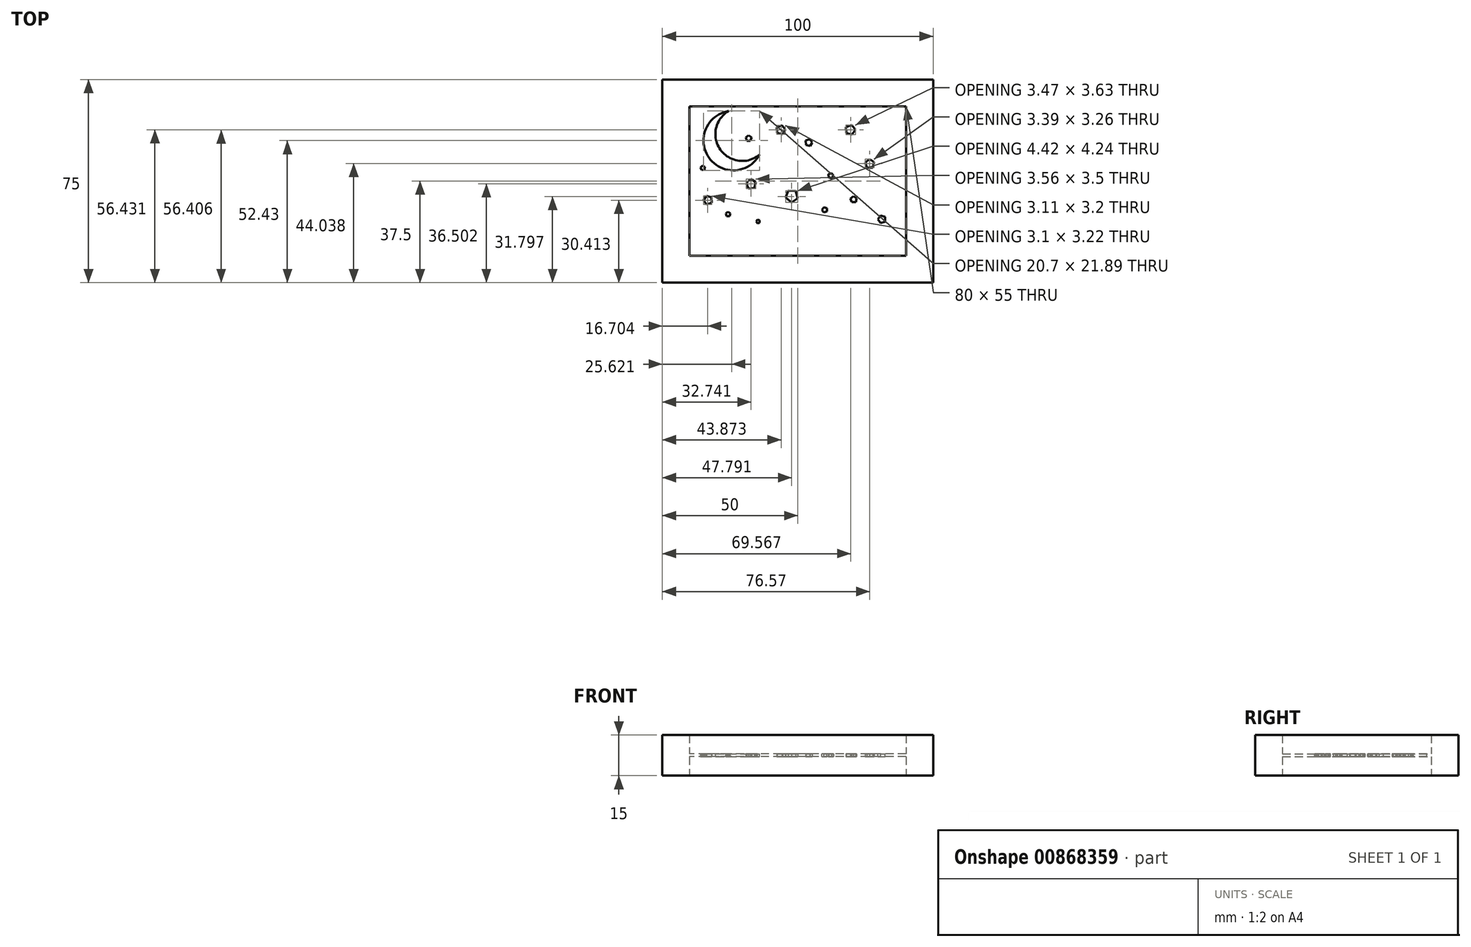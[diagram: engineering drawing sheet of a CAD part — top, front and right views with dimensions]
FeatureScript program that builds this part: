
annotation { "Feature Type Name" : "Feature", "Feature Type Description" : "" }
export const myFeature = defineFeature(function(context is Context, id is Id, definition is map)
    precondition{}
    {
        {
            var Q0;
            Q0=qCreatedBy(makeId("Top.planeOp"),FACE);
            var sketch = newSketch(context, id + "F0", { "sketchPlane" : qUnion([Q0])});
            skLineSegment(sketch, "E0.bottom", {"start": v(50, -37.5) * mm, "end": v(-50, -37.5) * mm});
            skLineSegment(sketch, "E0.top", {"start": v(50, 37.5) * mm, "end": v(-50, 37.5) * mm});
            skLineSegment(sketch, "E0.left", {"start": v(50, -37.5) * mm, "end": v(50, 37.5) * mm});
            skLineSegment(sketch, "E0.right", {"start": v(-50, -37.5) * mm, "end": v(-50, 37.5) * mm});
            skPoint(sketch, "E0.middle", {"position": v(0, 0) * mm});
            skLineSegment(sketch, "E1.bottom", {"start": v(40, -27.5) * mm, "end": v(-40, -27.5) * mm});
            skLineSegment(sketch, "E1.top", {"start": v(40, 27.5) * mm, "end": v(-40, 27.5) * mm});
            skLineSegment(sketch, "E1.left", {"start": v(40, -27.5) * mm, "end": v(40, 27.5) * mm});
            skLineSegment(sketch, "E1.right", {"start": v(-40, -27.5) * mm, "end": v(-40, 27.5) * mm});
            skSolve(sketch);
        }
        {
            var Q0;
            Q0=makeQuery(id+"F0.imprint","IMPRINT",FACE,{"disambiguationData":[TD([[makeQuery(id+"F0.imprint","IMPRINT",EDGE,{"derivedFrom":sQuery(id+"F0.wireOp",EDGE,"E0.bottom")}),-1.0]])]});
            extrude(context, id + "F1", {"entities" : qUnion([Q0]), "endBound" : BoundingType.SYMMETRIC, "depth" : 15 * mm, "offsetDistance" : 25 * mm});
        }
        {
            var Q0;
            Q0=qCreatedBy(makeId("Top.planeOp"),FACE);
            var sketch = newSketch(context, id + "F2", { "sketchPlane" : qUnion([Q0])});
            skLineSegment(sketch, "E2.bottom", {"start": v(42.5, -30) * mm, "end": v(-42.5, -30) * mm});
            skLineSegment(sketch, "E2.top", {"start": v(42.5, 30) * mm, "end": v(-42.5, 30) * mm});
            skLineSegment(sketch, "E2.left", {"start": v(42.5, -30) * mm, "end": v(42.5, 30) * mm});
            skLineSegment(sketch, "E2.right", {"start": v(-42.5, -30) * mm, "end": v(-42.5, 30) * mm});
            skPoint(sketch, "E2.middle", {"position": v(0, 0) * mm});
            skSolve(sketch);
        }
        {
            var Q0;
            Q0 = qSketchRegion(id + "F2", true);
            extrude(context, id + "F3", {"entities" : qUnion([Q0]), "operationType" : NewBodyOperationType.ADD, "endBound" : BoundingType.SYMMETRIC, "depth" : 1 * mm, "offsetDistance" : 25 * mm});
        }
        {
            var Q0;
            Q0=makeQuery(id+"F3.opExtrude","CAP_FACE",FACE,{"disambiguationData":[OSD([sQuery(id+"F2.wireOp",EDGE,"E2.bottom"),sQuery(id+"F2.wireOp",EDGE,"E2.top"),sQuery(id+"F2.wireOp",EDGE,"E2.left"),sQuery(id+"F2.wireOp",EDGE,"E2.right")])],"isStart":false});
            var sketch = newSketch(context, id + "F4", { "sketchPlane" : qUnion([Q0])});
            skCircle(sketch, "E3", {"center": v(-23.77, 14.99) * mm, "radius": 11.02 * mm});
            skCircle(sketch, "E4", {"center": v(-20.49, 17.33) * mm, "radius": 9.9 * mm});
            skSolve(sketch);
        }
        {
            var Q0;
            {var subQ0=sQuery(id+"F4.wireOp",EDGE,"E4");var subQ1=sQuery(id+"F4.wireOp",EDGE,"E3");var subQ2=makeQuery(id+"F4.imprint","INTERSECT",VERTEX,{"disambiguationData":[OD(0.0)],"derivedFrom":[subQ1,subQ0]});Q0=makeQuery(id+"F4.imprint","IMPRINT",FACE,{"disambiguationData":[TD([[makeQuery(id+"F4.imprint","IMPRINT",EDGE,{"disambiguationData":[TD([[subQ2,-1.0]])],"derivedFrom":subQ1}),1.0]])]});}
            extrude(context, id + "F5", {"entities" : qUnion([Q0]), "operationType" : NewBodyOperationType.REMOVE, "endBound" : BoundingType.SYMMETRIC, "oppositeDirection" : true, "depth" : 8 * mm, "offsetDistance" : 25 * mm});
        }
        {
            var Q0;
            Q0=makeQuery(id+"F3.opExtrude","CAP_FACE",FACE,{"disambiguationData":[OSD([sQuery(id+"F2.wireOp",EDGE,"E2.bottom"),sQuery(id+"F2.wireOp",EDGE,"E2.top"),sQuery(id+"F2.wireOp",EDGE,"E2.left"),sQuery(id+"F2.wireOp",EDGE,"E2.right")])],"isStart":false});
            var sketch = newSketch(context, id + "F6", { "sketchPlane" : qUnion([Q0])});
            skCircle(sketch, "E5.cCircle", {"center": v(-6.25, 18.9) * mm, "radius": 1.68 * mm, "construction": true});
            skLineSegment(sketch, "E5.0", {"start": v(-5.63, 17.33) * mm, "end": v(-7.55, 17.82) * mm});
            skLineSegment(sketch, "E5.1", {"start": v(-7.55, 17.82) * mm, "end": v(-7.68, 19.8) * mm});
            skLineSegment(sketch, "E5.2", {"start": v(-7.68, 19.8) * mm, "end": v(-5.84, 20.53) * mm});
            skLineSegment(sketch, "E5.3", {"start": v(-5.84, 20.53) * mm, "end": v(-4.57, 19) * mm});
            skLineSegment(sketch, "E5.4", {"start": v(-4.57, 19) * mm, "end": v(-5.63, 17.33) * mm});
            skCircle(sketch, "E6.cCircle", {"center": v(4.07, 14.2) * mm, "radius": 1.34 * mm, "construction": true});
            skLineSegment(sketch, "E6.0", {"start": v(4.54, 12.95) * mm, "end": v(3.02, 13.37) * mm});
            skLineSegment(sketch, "E6.1", {"start": v(3.02, 13.37) * mm, "end": v(2.95, 14.94) * mm});
            skLineSegment(sketch, "E6.2", {"start": v(2.95, 14.94) * mm, "end": v(4.42, 15.5) * mm});
            skLineSegment(sketch, "E6.3", {"start": v(4.42, 15.5) * mm, "end": v(5.4, 14.26) * mm});
            skLineSegment(sketch, "E6.4", {"start": v(5.4, 14.26) * mm, "end": v(4.54, 12.95) * mm});
            skCircle(sketch, "E7.cCircle", {"center": v(19.4, 18.9) * mm, "radius": 1.9 * mm, "construction": true});
            skLineSegment(sketch, "E7.0", {"start": v(17.83, 20) * mm, "end": v(19.95, 20.72) * mm});
            skLineSegment(sketch, "E7.1", {"start": v(19.95, 20.72) * mm, "end": v(21.3, 18.93) * mm});
            skLineSegment(sketch, "E7.2", {"start": v(21.3, 18.93) * mm, "end": v(20.02, 17.1) * mm});
            skLineSegment(sketch, "E7.3", {"start": v(20.02, 17.1) * mm, "end": v(17.87, 17.75) * mm});
            skLineSegment(sketch, "E7.4", {"start": v(17.87, 17.75) * mm, "end": v(17.83, 20) * mm});
            skCircle(sketch, "E8.cCircle", {"center": v(26.59, 6.38) * mm, "radius": 1.78 * mm, "construction": true});
            skLineSegment(sketch, "E8.0", {"start": v(27.68, 4.98) * mm, "end": v(25.59, 4.9) * mm});
            skLineSegment(sketch, "E8.1", {"start": v(25.59, 4.9) * mm, "end": v(24.88, 6.88) * mm});
            skLineSegment(sketch, "E8.2", {"start": v(24.88, 6.88) * mm, "end": v(26.53, 8.17) * mm});
            skLineSegment(sketch, "E8.3", {"start": v(26.53, 8.17) * mm, "end": v(28.27, 7) * mm});
            skLineSegment(sketch, "E8.4", {"start": v(28.27, 7) * mm, "end": v(27.68, 4.98) * mm});
            skCircle(sketch, "E9.cCircle", {"center": v(12.2, 2) * mm, "radius": 1 * mm, "construction": true});
            skLineSegment(sketch, "E9.0", {"start": v(11.42, 1.38) * mm, "end": v(11.36, 2.56) * mm});
            skLineSegment(sketch, "E9.1", {"start": v(11.36, 2.56) * mm, "end": v(12.47, 2.97) * mm});
            skLineSegment(sketch, "E9.2", {"start": v(12.47, 2.97) * mm, "end": v(13.2, 2.05) * mm});
            skLineSegment(sketch, "E9.3", {"start": v(13.2, 2.05) * mm, "end": v(12.55, 1.07) * mm});
            skLineSegment(sketch, "E9.4", {"start": v(12.55, 1.07) * mm, "end": v(11.42, 1.38) * mm});
            skCircle(sketch, "E10.cCircle", {"center": v(-17.2, -1.12) * mm, "radius": 1.88 * mm, "construction": true});
            skLineSegment(sketch, "E10.0", {"start": v(-15.95, -2.53) * mm, "end": v(-18.15, -2.75) * mm});
            skLineSegment(sketch, "E10.1", {"start": v(-18.15, -2.75) * mm, "end": v(-19.04, -0.72) * mm});
            skLineSegment(sketch, "E10.2", {"start": v(-19.04, -0.72) * mm, "end": v(-17.39, 0.75) * mm});
            skLineSegment(sketch, "E10.3", {"start": v(-17.39, 0.75) * mm, "end": v(-15.48, -0.37) * mm});
            skLineSegment(sketch, "E10.4", {"start": v(-15.48, -0.37) * mm, "end": v(-15.95, -2.53) * mm});
            skCircle(sketch, "E11.cCircle", {"center": v(-18.14, 15.77) * mm, "radius": 1.13 * mm, "construction": true});
            skLineSegment(sketch, "E11.0", {"start": v(-17.51, 14.83) * mm, "end": v(-18.84, 14.88) * mm});
            skLineSegment(sketch, "E11.1", {"start": v(-18.84, 14.88) * mm, "end": v(-19.2, 16.16) * mm});
            skLineSegment(sketch, "E11.2", {"start": v(-19.2, 16.16) * mm, "end": v(-18.1, 16.9) * mm});
            skLineSegment(sketch, "E11.3", {"start": v(-18.1, 16.9) * mm, "end": v(-17.05, 16.07) * mm});
            skLineSegment(sketch, "E11.4", {"start": v(-17.05, 16.07) * mm, "end": v(-17.51, 14.83) * mm});
            skCircle(sketch, "E12.cCircle", {"center": v(-2.19, -5.5) * mm, "radius": 2.32 * mm, "construction": true});
            skLineSegment(sketch, "E12.0", {"start": v(0, -6.28) * mm, "end": v(-2.26, -7.82) * mm});
            skLineSegment(sketch, "E12.1", {"start": v(-2.26, -7.82) * mm, "end": v(-4.42, -6.16) * mm});
            skLineSegment(sketch, "E12.2", {"start": v(-4.42, -6.16) * mm, "end": v(-3.5, -3.58) * mm});
            skLineSegment(sketch, "E12.3", {"start": v(-3.5, -3.58) * mm, "end": v(-0.77, -3.66) * mm});
            skLineSegment(sketch, "E12.4", {"start": v(-0.77, -3.66) * mm, "end": v(0, -6.28) * mm});
            skCircle(sketch, "E13.cCircle", {"center": v(20.65, -6.75) * mm, "radius": 1.22 * mm, "construction": true});
            skLineSegment(sketch, "E13.0", {"start": v(21.43, -7.7) * mm, "end": v(20, -7.79) * mm});
            skLineSegment(sketch, "E13.1", {"start": v(20, -7.79) * mm, "end": v(19.46, -6.45) * mm});
            skLineSegment(sketch, "E13.2", {"start": v(19.46, -6.45) * mm, "end": v(20.56, -5.53) * mm});
            skLineSegment(sketch, "E13.3", {"start": v(20.56, -5.53) * mm, "end": v(21.78, -6.3) * mm});
            skLineSegment(sketch, "E13.4", {"start": v(21.78, -6.3) * mm, "end": v(21.43, -7.7) * mm});
            skCircle(sketch, "E14.cCircle", {"center": v(-33.15, -7.07) * mm, "radius": 1.7 * mm, "construction": true});
            skLineSegment(sketch, "E14.0", {"start": v(-31.75, -8) * mm, "end": v(-33.61, -8.7) * mm});
            skLineSegment(sketch, "E14.1", {"start": v(-33.61, -8.7) * mm, "end": v(-34.84, -7.13) * mm});
            skLineSegment(sketch, "E14.2", {"start": v(-34.84, -7.13) * mm, "end": v(-33.74, -5.48) * mm});
            skLineSegment(sketch, "E14.3", {"start": v(-33.74, -5.48) * mm, "end": v(-31.83, -6.02) * mm});
            skLineSegment(sketch, "E14.4", {"start": v(-31.83, -6.02) * mm, "end": v(-31.75, -8) * mm});
            skCircle(sketch, "E15.cCircle", {"center": v(-35.03, 4.82) * mm, "radius": 0.88 * mm, "construction": true});
            skLineSegment(sketch, "E15.0", {"start": v(-34.4, 4.2) * mm, "end": v(-35.43, 4.03) * mm});
            skLineSegment(sketch, "E15.1", {"start": v(-35.43, 4.03) * mm, "end": v(-35.9, 4.96) * mm});
            skLineSegment(sketch, "E15.2", {"start": v(-35.9, 4.96) * mm, "end": v(-35.17, 5.7) * mm});
            skLineSegment(sketch, "E15.3", {"start": v(-35.17, 5.7) * mm, "end": v(-34.24, 5.22) * mm});
            skLineSegment(sketch, "E15.4", {"start": v(-34.24, 5.22) * mm, "end": v(-34.4, 4.2) * mm});
            skSolve(sketch);
        }
        {
            var Q0;
            Q0=makeQuery(id+"F6.imprint","IMPRINT",FACE,{"disambiguationData":[TD([[makeQuery(id+"F6.imprint","IMPRINT",EDGE,{"derivedFrom":sQuery(id+"F6.wireOp",EDGE,"E14.0")}),-1.0]])]});
            var Q1;
            Q1=makeQuery(id+"F6.imprint","IMPRINT",FACE,{"disambiguationData":[TD([[makeQuery(id+"F6.imprint","IMPRINT",EDGE,{"derivedFrom":sQuery(id+"F6.wireOp",EDGE,"E10.0")}),-1.0]])]});
            var Q2;
            Q2=makeQuery(id+"F6.imprint","IMPRINT",FACE,{"disambiguationData":[TD([[makeQuery(id+"F6.imprint","IMPRINT",EDGE,{"derivedFrom":sQuery(id+"F6.wireOp",EDGE,"E15.0")}),-1.0]])]});
            var Q3;
            Q3=makeQuery(id+"F6.imprint","IMPRINT",FACE,{"disambiguationData":[TD([[makeQuery(id+"F6.imprint","IMPRINT",EDGE,{"derivedFrom":sQuery(id+"F6.wireOp",EDGE,"E12.0")}),-1.0]])]});
            var Q4;
            Q4=makeQuery(id+"F6.imprint","IMPRINT",FACE,{"disambiguationData":[TD([[makeQuery(id+"F6.imprint","IMPRINT",EDGE,{"derivedFrom":sQuery(id+"F6.wireOp",EDGE,"E8.0")}),-1.0]])]});
            var Q5;
            Q5=makeQuery(id+"F6.imprint","IMPRINT",FACE,{"disambiguationData":[TD([[makeQuery(id+"F6.imprint","IMPRINT",EDGE,{"derivedFrom":sQuery(id+"F6.wireOp",EDGE,"E13.0")}),-1.0]])]});
            var Q6;
            Q6=makeQuery(id+"F6.imprint","IMPRINT",FACE,{"disambiguationData":[TD([[makeQuery(id+"F6.imprint","IMPRINT",EDGE,{"derivedFrom":sQuery(id+"F6.wireOp",EDGE,"E9.0")}),-1.0]])]});
            var Q7;
            Q7=makeQuery(id+"F6.imprint","IMPRINT",FACE,{"disambiguationData":[TD([[makeQuery(id+"F6.imprint","IMPRINT",EDGE,{"derivedFrom":sQuery(id+"F6.wireOp",EDGE,"E6.0")}),-1.0]])]});
            var Q8;
            Q8=makeQuery(id+"F6.imprint","IMPRINT",FACE,{"disambiguationData":[TD([[makeQuery(id+"F6.imprint","IMPRINT",EDGE,{"derivedFrom":sQuery(id+"F6.wireOp",EDGE,"E7.0")}),-1.0]])]});
            var Q9;
            Q9=makeQuery(id+"F6.imprint","IMPRINT",FACE,{"disambiguationData":[TD([[makeQuery(id+"F6.imprint","IMPRINT",EDGE,{"derivedFrom":sQuery(id+"F6.wireOp",EDGE,"E5.0")}),-1.0]])]});
            var Q10;
            Q10=makeQuery(id+"F6.imprint","IMPRINT",FACE,{"disambiguationData":[TD([[makeQuery(id+"F6.imprint","IMPRINT",EDGE,{"derivedFrom":sQuery(id+"F6.wireOp",EDGE,"E11.0")}),-1.0]])]});
            extrude(context, id + "F7", {"entities" : qUnion([Q0, Q1, Q2, Q3, Q4, Q5, Q6, Q7, Q8, Q9, Q10]), "operationType" : NewBodyOperationType.REMOVE, "endBound" : BoundingType.SYMMETRIC, "depth" : 8 * mm, "offsetDistance" : 25 * mm});
        }
        {
            var Q0;
            Q0=makeQuery(id+"F3.opExtrude","CAP_FACE",FACE,{"disambiguationData":[OSD([sQuery(id+"F2.wireOp",EDGE,"E2.bottom"),sQuery(id+"F2.wireOp",EDGE,"E2.top"),sQuery(id+"F2.wireOp",EDGE,"E2.left"),sQuery(id+"F2.wireOp",EDGE,"E2.right")])],"isStart":false});
            var sketch = newSketch(context, id + "F8", { "sketchPlane" : qUnion([Q0])});
            skCircle(sketch, "E16.cCircle", {"center": v(-25.7, -12.22) * mm, "radius": 0.72 * mm, "construction": true});
            skLineSegment(sketch, "E16.0", {"start": v(-25.18, -12.94) * mm, "end": v(-26.23, -12.94) * mm});
            skLineSegment(sketch, "E16.1", {"start": v(-26.23, -12.94) * mm, "end": v(-26.56, -11.94) * mm});
            skLineSegment(sketch, "E16.2", {"start": v(-26.56, -11.94) * mm, "end": v(-25.7, -11.32) * mm});
            skLineSegment(sketch, "E16.3", {"start": v(-25.7, -11.32) * mm, "end": v(-24.86, -11.94) * mm});
            skLineSegment(sketch, "E16.4", {"start": v(-24.86, -11.94) * mm, "end": v(-25.18, -12.94) * mm});
            skPoint(sketch, "E16.0.midPoint", {"position": v(-25.7, -12.94) * mm});
            skCircle(sketch, "E17.cCircle", {"center": v(-14.66, -14.91) * mm, "radius": 0.6 * mm, "construction": true});
            skLineSegment(sketch, "E17.0", {"start": v(-14.07, -14.48) * mm, "end": v(-14.07, -15.34) * mm});
            skLineSegment(sketch, "E17.1", {"start": v(-14.07, -15.34) * mm, "end": v(-14.88, -15.6) * mm});
            skLineSegment(sketch, "E17.2", {"start": v(-14.88, -15.6) * mm, "end": v(-15.4, -14.91) * mm});
            skLineSegment(sketch, "E17.3", {"start": v(-15.4, -14.91) * mm, "end": v(-14.88, -14.22) * mm});
            skLineSegment(sketch, "E17.4", {"start": v(-14.88, -14.22) * mm, "end": v(-14.07, -14.48) * mm});
            skPoint(sketch, "E17.0.midPoint", {"position": v(-14.07, -14.91) * mm});
            skCircle(sketch, "E18.cCircle", {"center": v(9.97, -10.64) * mm, "radius": 0.81 * mm, "construction": true});
            skLineSegment(sketch, "E18.0", {"start": v(10.78, -10.05) * mm, "end": v(10.78, -11.23) * mm});
            skLineSegment(sketch, "E18.1", {"start": v(10.78, -11.23) * mm, "end": v(9.66, -11.6) * mm});
            skLineSegment(sketch, "E18.2", {"start": v(9.66, -11.6) * mm, "end": v(8.96, -10.64) * mm});
            skLineSegment(sketch, "E18.3", {"start": v(8.96, -10.64) * mm, "end": v(9.66, -9.68) * mm});
            skLineSegment(sketch, "E18.4", {"start": v(9.66, -9.68) * mm, "end": v(10.78, -10.05) * mm});
            skPoint(sketch, "E18.0.midPoint", {"position": v(10.78, -10.64) * mm});
            skCircle(sketch, "E19.cCircle", {"center": v(31.06, -14.09) * mm, "radius": 1.22 * mm, "construction": true});
            skLineSegment(sketch, "E19.0", {"start": v(32.28, -13.2) * mm, "end": v(32.28, -14.97) * mm});
            skLineSegment(sketch, "E19.1", {"start": v(32.28, -14.97) * mm, "end": v(30.6, -15.52) * mm});
            skLineSegment(sketch, "E19.2", {"start": v(30.6, -15.52) * mm, "end": v(29.56, -14.09) * mm});
            skLineSegment(sketch, "E19.3", {"start": v(29.56, -14.09) * mm, "end": v(30.6, -12.66) * mm});
            skLineSegment(sketch, "E19.4", {"start": v(30.6, -12.66) * mm, "end": v(32.28, -13.2) * mm});
            skPoint(sketch, "E19.0.midPoint", {"position": v(32.28, -14.09) * mm});
            skSolve(sketch);
        }
        {
            var Q0;
            Q0=makeQuery(id+"F8.imprint","IMPRINT",FACE,{"disambiguationData":[TD([[makeQuery(id+"F8.imprint","IMPRINT",EDGE,{"derivedFrom":sQuery(id+"F8.wireOp",EDGE,"E16.0")}),-1.0]])]});
            var Q1;
            Q1=makeQuery(id+"F8.imprint","IMPRINT",FACE,{"disambiguationData":[TD([[makeQuery(id+"F8.imprint","IMPRINT",EDGE,{"derivedFrom":sQuery(id+"F8.wireOp",EDGE,"E17.0")}),-1.0]])]});
            var Q2;
            Q2=makeQuery(id+"F8.imprint","IMPRINT",FACE,{"disambiguationData":[TD([[makeQuery(id+"F8.imprint","IMPRINT",EDGE,{"derivedFrom":sQuery(id+"F8.wireOp",EDGE,"E19.0")}),-1.0]])]});
            var Q3;
            Q3=makeQuery(id+"F8.imprint","IMPRINT",FACE,{"disambiguationData":[TD([[makeQuery(id+"F8.imprint","IMPRINT",EDGE,{"derivedFrom":sQuery(id+"F8.wireOp",EDGE,"E18.0")}),-1.0]])]});
            extrude(context, id + "F9", {"entities" : qUnion([Q0, Q1, Q2, Q3]), "operationType" : NewBodyOperationType.REMOVE, "oppositeDirection" : true, "depth" : 2 * mm, "offsetDistance" : 25 * mm});
        }
    });
